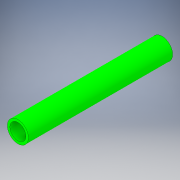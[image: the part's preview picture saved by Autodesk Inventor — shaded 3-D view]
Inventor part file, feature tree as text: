
AUTODESK INVENTOR PART (.ipt)
format: ipt  version: 2018.2 (Build 222227000, 227)  size: 107,008 bytes
history: native  units: in
note: dims shown in document units (in); Inventor stores cm internally (conversion verified against a paired STEP export)
features: extrude x1, sketch x1
ambient origin geometry x8: Origin, YZ Plane, XZ Plane, XY Plane, X Axis, Y Axis, Z Axis, Center Point
bodies: Solid1 (feature_tree)
feature tree (2):
  extrude  "Extrusion1"  Depth=9.0in
  sketch  "Sketch1"  dims[d0=1.315in d1=1.0in d2=9.0in d3=0.0in]
